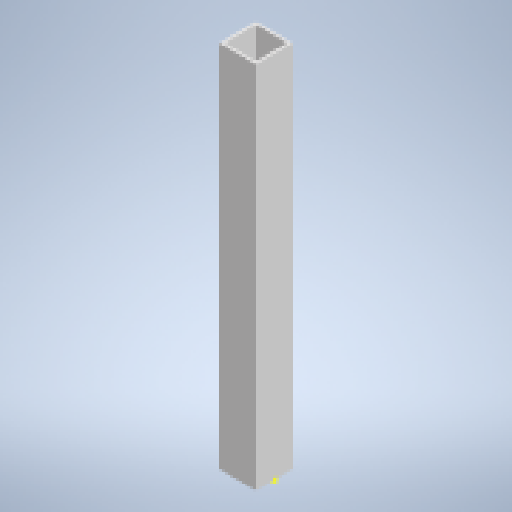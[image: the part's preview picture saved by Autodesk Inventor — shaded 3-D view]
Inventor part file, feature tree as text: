
AUTODESK INVENTOR PART (.ipt)
format: ipt  version: 2025 (Build 290162000, 162)  size: 253,952 bytes
history: native  units: in
note: dims shown in document units (in); Inventor stores cm internally (conversion verified against a paired STEP export)
features: sketch x2, extrude x1
ambient origin geometry x8: Origin, YZ Plane, XZ Plane, XY Plane, X Axis, Y Axis, Z Axis, Center Point
bodies: Solid1 (feature_tree)
feature tree (3):
  extrude  "Extrusion1"  Depth=1.5748in
  sketch  "Sketch2"  dims[d2=1.3386in d3=1.3386in d4=0.1181in d5=15.3543in d6=0.0in]
  sketch  "Sketch1"  dims[d0=1.5748in d1=1.5748in]
